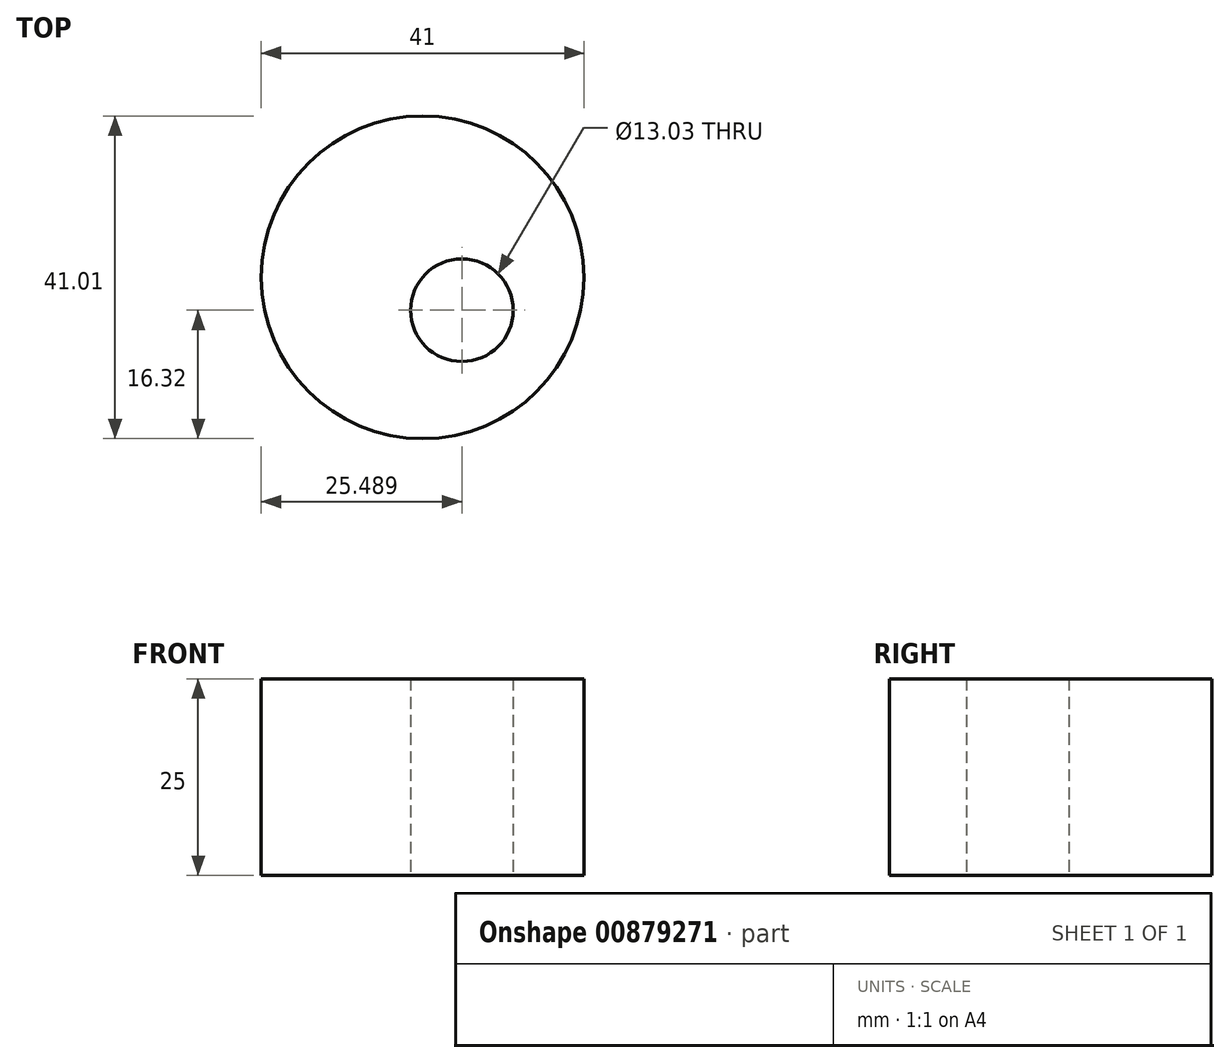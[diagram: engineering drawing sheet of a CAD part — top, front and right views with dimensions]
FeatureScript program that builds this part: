
annotation { "Feature Type Name" : "Feature", "Feature Type Description" : "" }
export const myFeature = defineFeature(function(context is Context, id is Id, definition is map)
    precondition{}
    {
        {
            var Q0;
            Q0=qCreatedBy(makeId("Top.planeOp"),FACE);
            var sketch = newSketch(context, id + "F0", { "sketchPlane" : qUnion([Q0])});
            skCircle(sketch, "E0", {"center": v(25.06, 0) * mm, "radius": 6.51 * mm});
            skCircle(sketch, "E1", {"center": v(20.07, 4.19) * mm, "radius": 20.5 * mm});
            skSolve(sketch);
        }
        {
            var Q0;
            Q0=makeQuery(id+"F0.imprint","IMPRINT",FACE,{"disambiguationData":[TD([[makeQuery(id+"F0.imprint","IMPRINT",EDGE,{"derivedFrom":sQuery(id+"F0.wireOp",EDGE,"E0")}),-1.0]])]});
            extrude(context, id + "F1", {"entities" : qUnion([Q0]), "depth" : 25 * mm, "offsetDistance" : 25 * mm});
        }
    });
